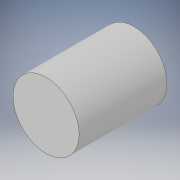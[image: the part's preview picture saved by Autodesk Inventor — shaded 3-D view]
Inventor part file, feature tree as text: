
AUTODESK INVENTOR PART (.ipt)
format: ipt  version: 2017 (Build 210142000, 142)  size: 88,576 bytes
history: native  units: in
note: dims shown in document units (in); Inventor stores cm internally (conversion verified against a paired STEP export)
features: extrude x1, sketch x1
ambient origin geometry x8: Origin, YZ Plane, XZ Plane, XY Plane, X Axis, Y Axis, Z Axis, Center Point
bodies: Solid1 (feature_tree)
feature tree (2):
  extrude  "Extrusion1"  Depth=0.25in TaperAngle=0.0deg
  sketch  "Sketch1"  dims[d0=0.188in d1=0.25in d2=0.0in]
